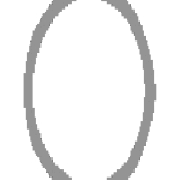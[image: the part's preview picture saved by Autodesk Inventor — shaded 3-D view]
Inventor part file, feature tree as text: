
AUTODESK INVENTOR PART (.ipt)
format: ipt  version: 2021 (Build 250183000, 183)  size: 109,056 bytes
history: native  units: in
note: dims shown in document units (in); Inventor stores cm internally (conversion verified against a paired STEP export)
features: other x4, sketch x3, plane x1
ambient origin geometry x8: Origin, YZ Plane, XZ Plane, XY Plane, X Axis, Y Axis, Z Axis, Center Point
bodies: Solid1 (feature_tree), Body (feature_tree)
feature tree (8):
  other  "Driven Length"
  other  "Frame Generator"
  other  "Start Plane"
  other  "End Plane"
  sketch  "Sketch"  dims[d2=36.7214in d4=-0.0in d5=36.7214in d6=0.12in d7=0.0in d10=90.0deg d9=36.7214in]
  sketch  "Sketch4"  dims[d0=1.0in]
  plane  "Work Plane4"
  sketch  "Sketch5"  dims[d1=0.065in]
